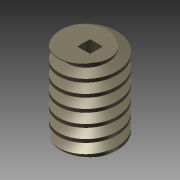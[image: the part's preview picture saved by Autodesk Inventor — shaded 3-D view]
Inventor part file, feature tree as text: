
AUTODESK INVENTOR PART (.ipt)
format: ipt  version: 2013 (Build 170138000, 138)  size: 1,001,984 bytes
history: native  units: mm (DEFAULTED — no unit token found)
features: other x2, plane x2, imported_body x1, sketch x1, extrude x1
ambient origin geometry x8: Origin, YZ Plane, XZ Plane, XY Plane, X Axis, Y Axis, Z Axis, Center Point
bodies: Solid1 (feature_tree)
feature tree (7):
  imported_body  "Base1"
  other  "Work Axis1"
  plane  "Work Plane1"
  plane  "Work Plane2"
  sketch  "Sketch1"  dims[d3=25.4mm d4=0.0mm d5=0.0mm d6=0.0mm]
  other  "Srf1"
  extrude  "ExtrusionSrf1"  TaperAngle=0.0deg  [1 undecoded]
note: 1 required parameter value undecoded (feature->parameter linkage not recoverable at this tier; creation-order binding heuristic only, values carry confidence <= 0.55)
